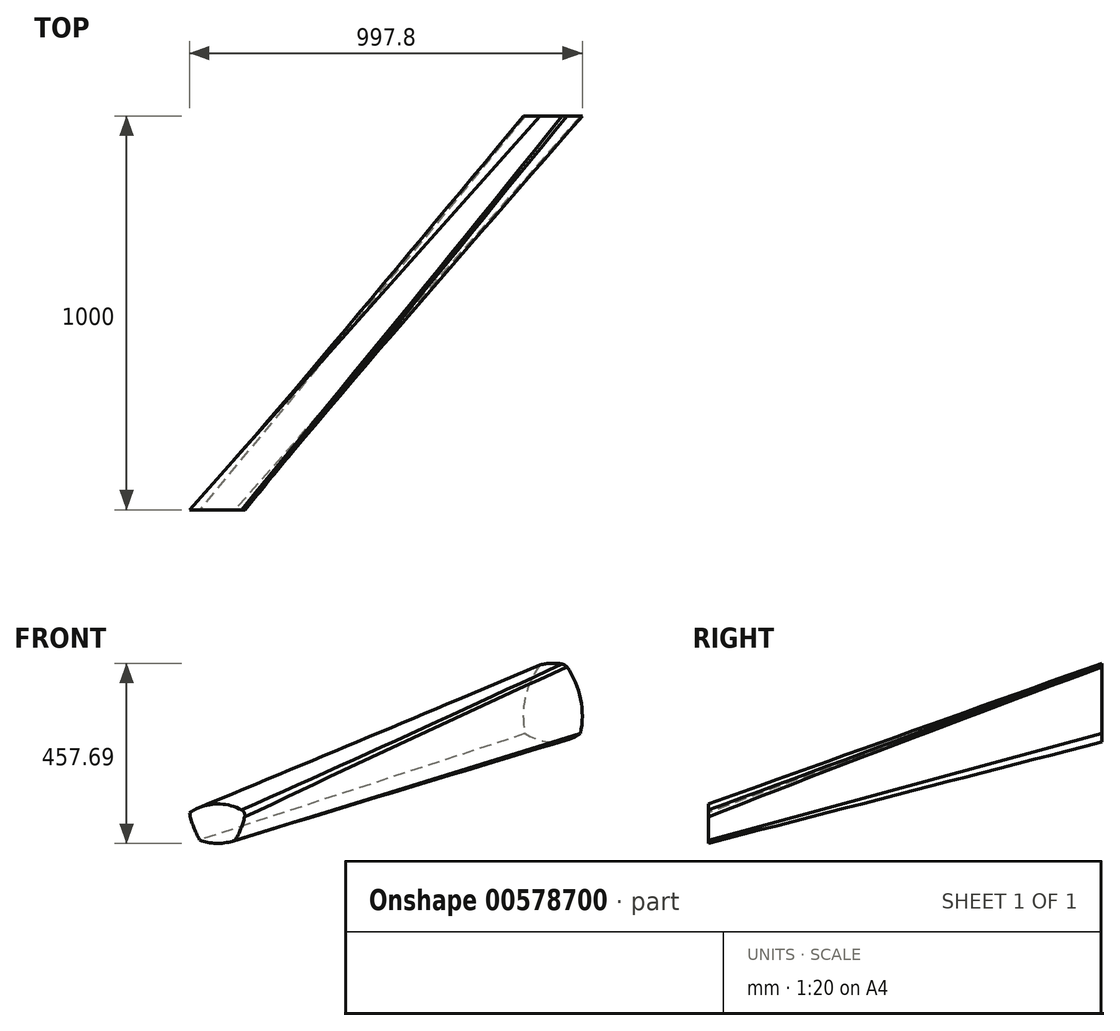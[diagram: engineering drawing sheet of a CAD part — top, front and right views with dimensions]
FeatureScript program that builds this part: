
annotation { "Feature Type Name" : "Feature", "Feature Type Description" : "" }
export const myFeature = defineFeature(function(context is Context, id is Id, definition is map)
    precondition{}
    {
        {
            var Q0;
            Q0=qCreatedBy(makeId("Front.planeOp"),FACE);
            var sketch = newSketch(context, id + "F0", { "sketchPlane" : qUnion([Q0])});
            skPoint(sketch, "E0", {"position": v(-20, 200) * mm});
            skLineSegment(sketch, "E1", {"start": v(-125.88, 200) * mm, "end": v(85.88, 200) * mm, "construction": true});
            skLineSegment(sketch, "E2", {"start": v(-20, 456.4) * mm, "end": v(-20, -56.4) * mm, "construction": true});
            skArc(sketch, "E3", {"start": v(11.88, 295.93) * mm, "mid": v(-20, 300) * mm, "end": v(-51.88, 295.93) * mm});
            skArc(sketch, "E4", {"start": v(-90, 121.05) * mm, "mid": v(-20, 100) * mm, "end": v(50, 121.05) * mm});
            skArc(sketch, "E5", {"start": v(-51.88, 295.93) * mm, "mid": v(-90.09, 212.66) * mm, "end": v(-90, 121.05) * mm});
            skArc(sketch, "E6", {"start": v(50, 121.05) * mm, "mid": v(50.09, 212.66) * mm, "end": v(11.88, 295.93) * mm});
            skLineSegment(sketch, "E7", {"start": v(-159.14, 167.06) * mm, "end": v(119.14, 167.06) * mm, "construction": true});
            skSolve(sketch);
        }
        {
            var Q0;
            Q0=qCreatedBy(makeId("Front.planeOp"),FACE);
            cPlane(context, id + "F1", {"entities" : qUnion([Q0]), "cplaneType" : CPlaneType.OFFSET, "offset" : 1000 * mm, "width" : 150 * mm, "height" : 150 * mm});
        }
        {
            var Q0;
            Q0=qCreatedBy(id+"F1.planeOp",FACE);
            var sketch = newSketch(context, id + "F2", { "sketchPlane" : qUnion([Q0])});
            skPoint(sketch, "E8", {"position": v(-871.63, -107.69) * mm});
            skLineSegment(sketch, "E9", {"start": v(-894.4, -107.69) * mm, "end": v(-848.87, -107.69) * mm, "construction": true});
            skLineSegment(sketch, "E10", {"start": v(-871.63, 156.44) * mm, "end": v(-871.63, -371.82) * mm, "construction": true});
            skArc(sketch, "E11", {"start": v(-800.27, -79.1) * mm, "mid": v(-871.69, -57.7) * mm, "end": v(-942.8, -80.08) * mm});
            skArc(sketch, "E12", {"start": v(-916.86, -149.04) * mm, "mid": v(-871.94, -157.68) * mm, "end": v(-826.87, -149.84) * mm});
            skArc(sketch, "E13", {"start": v(-942.8, -80.08) * mm, "mid": v(-932.8, -115.68) * mm, "end": v(-916.86, -149.04) * mm});
            skArc(sketch, "E14", {"start": v(-826.87, -149.84) * mm, "mid": v(-810.45, -115.64) * mm, "end": v(-800.27, -79.1) * mm});
            skLineSegment(sketch, "E15", {"start": v(-1012.73, -39.6) * mm, "end": v(-730.53, -39.6) * mm, "construction": true});
            skSolve(sketch);
        }
        {
            var Q0;
            Q0 = qSketchRegion(id + "F0", true);
            var Q1;
            Q1 = qSketchRegion(id + "F2", true);
            loft(context, id + "F3", {"sheetProfilesArray" : [{ "sheetProfileEntities" : qUnion([Q0]) }, { "sheetProfileEntities" : qUnion([Q1]) }]});
        }
        {
            var Q0;
            Q0=makeQuery(id+"F3.opLoft","SWEPT_EDGE",EDGE,{"disambiguationData":[OSD([sQuery(id+"F0.wireOp",EDGE,"E3"),sQuery(id+"F0.wireOp",EDGE,"E6"),sQuery(id+"F2.wireOp",EDGE,"E11"),sQuery(id+"F2.wireOp",EDGE,"E14")])]});
            fillet(context, id + "F4", {"entities" : qUnion([Q0]), "radius" : 20 * mm, "tangentPropagation" : true, "allowEdgeOverflow" : false});
        }
    });
